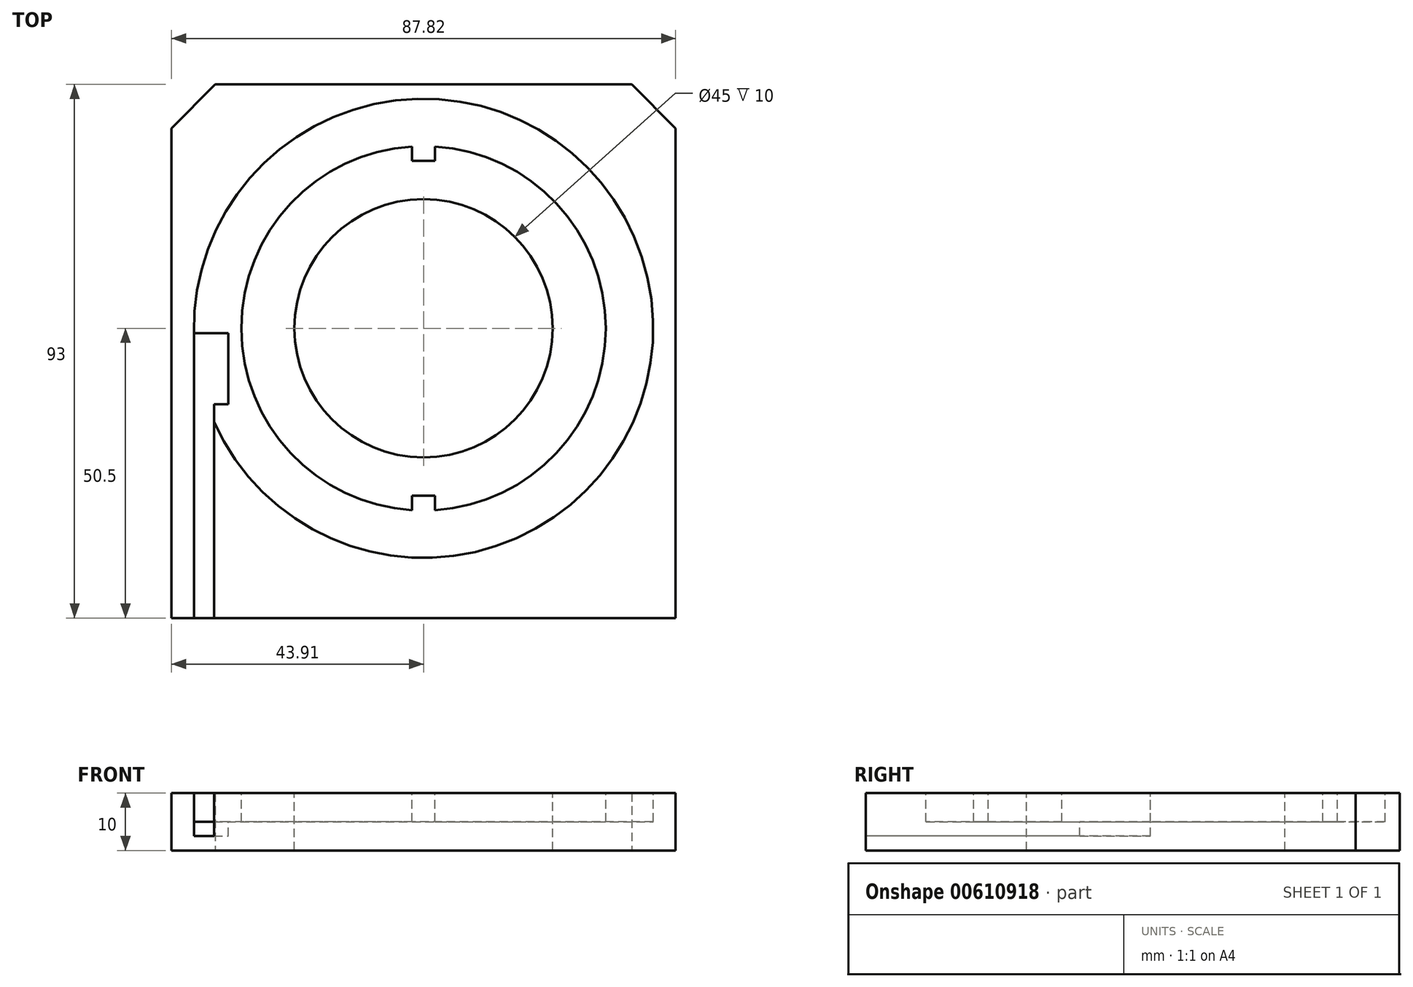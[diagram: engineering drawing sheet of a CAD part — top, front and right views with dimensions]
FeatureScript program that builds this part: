
annotation { "Feature Type Name" : "Feature", "Feature Type Description" : "" }
export const myFeature = defineFeature(function(context is Context, id is Id, definition is map)
    precondition{}
    {
        {
            var Q0;
            Q0=qCreatedBy(makeId("Top.planeOp"),FACE);
            var sketch = newSketch(context, id + "F0", { "sketchPlane" : qUnion([Q0])});
            skLineSegment(sketch, "E0.bottom", {"start": v(36.28, 46.5) * mm, "end": v(-36.28, 46.5) * mm});
            skLineSegment(sketch, "E0.top", {"start": v(43.92, -46.5) * mm, "end": v(-43.91, -46.5) * mm});
            skLineSegment(sketch, "E0.left", {"start": v(43.91, 38.86) * mm, "end": v(43.92, -46.5) * mm});
            skLineSegment(sketch, "E0.right", {"start": v(-43.92, 38.86) * mm, "end": v(-43.91, -46.5) * mm});
            skPoint(sketch, "E0.middle", {"position": v(0, 0) * mm});
            skLineSegment(sketch, "E1", {"start": v(-36.28, 46.5) * mm, "end": v(-43.92, 38.86) * mm});
            skLineSegment(sketch, "E2", {"start": v(36.28, 46.5) * mm, "end": v(43.92, 38.86) * mm});
            skPoint(sketch, "E3.orphan", {"position": v(-43.92, 46.5) * mm});
            skPoint(sketch, "E4.orphan", {"position": v(43.91, 46.5) * mm});
            skPoint(sketch, "E5.center.orphan", {"position": v(0, 4) * mm});
            skSolve(sketch);
        }
        {
            var Q0;
            Q0 = qSketchRegion(id + "F0", true);
            extrude(context, id + "F1", {"entities" : qUnion([Q0]), "depth" : 10 * mm, "offsetDistance" : 25 * mm});
        }
        {
            var Q0;
            Q0=makeQuery(id+"F1.opExtrude","CAP_FACE",FACE,{"disambiguationData":[OSD([sQuery(id+"F0.wireOp",EDGE,"E0.bottom"),sQuery(id+"F0.wireOp",EDGE,"E0.top"),sQuery(id+"F0.wireOp",EDGE,"E0.left"),sQuery(id+"F0.wireOp",EDGE,"E0.right"),sQuery(id+"F0.wireOp",EDGE,"E1"),sQuery(id+"F0.wireOp",EDGE,"E2")])],"isStart":false});
            var sketch = newSketch(context, id + "F2", { "sketchPlane" : qUnion([Q0])});
            skLineSegment(sketch, "E6", {"start": v(-43.92, 24) * mm, "end": v(43.91, 24) * mm, "construction": true});
            skCircle(sketch, "E7", {"center": v(0, 4) * mm, "radius": 20 * mm, "construction": true});
            skCircle(sketch, "E8", {"center": v(0, 4) * mm, "radius": 22.5 * mm});
            skCircle(sketch, "E9", {"center": v(0, 4) * mm, "radius": 40 * mm});
            skArc(sketch, "E10", {"start": v(2, -27.69) * mm, "mid": v(31.75, 4) * mm, "end": v(2, 35.69) * mm});
            skLineSegment(sketch, "E11", {"start": v(-2, 35.69) * mm, "end": v(-2, 33.15) * mm});
            skLineSegment(sketch, "E12", {"start": v(-2, 33.15) * mm, "end": v(2, 33.15) * mm});
            skLineSegment(sketch, "E13", {"start": v(2, 33.15) * mm, "end": v(2, 35.69) * mm});
            skLineSegment(sketch, "E14", {"start": v(0, 46.5) * mm, "end": v(0, -46.5) * mm, "construction": true});
            skLineSegment(sketch, "E15", {"start": v(-2, -27.69) * mm, "end": v(-2, -25.15) * mm});
            skLineSegment(sketch, "E16", {"start": v(-2, -25.15) * mm, "end": v(2, -25.15) * mm});
            skLineSegment(sketch, "E17", {"start": v(2, -25.15) * mm, "end": v(2, -27.69) * mm});
            skArc(sketch, "E18.trimOffspring", {"start": v(-2, 35.69) * mm, "mid": v(-31.75, 4) * mm, "end": v(-2, -27.69) * mm});
            skSolve(sketch);
        }
        {
            var Q0;
            Q0=makeQuery(id+"F2.imprint","IMPRINT",FACE,{"disambiguationData":[TD([[makeQuery(id+"F2.imprint","IMPRINT",EDGE,{"derivedFrom":sQuery(id+"F2.wireOp",EDGE,"E9")}),-1.0]])]});
            var sketch = newSketch(context, id + "F3", { "sketchPlane" : qUnion([Q0])});
            skLineSegment(sketch, "E19", {"start": v(-40, 3.11) * mm, "end": v(-40, -46.5) * mm, "construction": true});
            skLineSegment(sketch, "E20", {"start": v(-44.37, 3.11) * mm, "end": v(-20, 3.11) * mm, "construction": true});
            skLineSegment(sketch, "E21.top", {"start": v(-40, -46.5) * mm, "end": v(-36.52, -46.5) * mm});
            skLineSegment(sketch, "E21.left", {"start": v(-40, 3.11) * mm, "end": v(-40, -46.5) * mm});
            skLineSegment(sketch, "E21.right", {"start": v(-36.52, -9.2) * mm, "end": v(-36.52, -46.5) * mm});
            skLineSegment(sketch, "E22", {"start": v(-36.52, -9.2) * mm, "end": v(-34, -9.2) * mm});
            skLineSegment(sketch, "E23", {"start": v(-34, -9.2) * mm, "end": v(-34, 3.11) * mm});
            skLineSegment(sketch, "E24", {"start": v(-40, 3.11) * mm, "end": v(-34, 3.11) * mm});
            skPoint(sketch, "E25.end.orphan", {"position": v(-33.34, -110.36) * mm});
            skPoint(sketch, "E25.start.orphan", {"position": v(-40, -110.36) * mm});
            skSolve(sketch);
        }
        {
            var Q0;
            Q0 = qSketchRegion(id + "F3", true);
            extrude(context, id + "F4", {"entities" : qUnion([Q0]), "operationType" : NewBodyOperationType.REMOVE, "oppositeDirection" : true, "depth" : 7.5 * mm, "offsetDistance" : 25 * mm});
        }
        {
            var Q0;
            Q0=makeQuery(id+"F2.imprint","IMPRINT",FACE,{"disambiguationData":[TD([[makeQuery(id+"F2.imprint","IMPRINT",EDGE,{"derivedFrom":sQuery(id+"F2.wireOp",EDGE,"E8")}),1.0]])]});
            extrude(context, id + "F5", {"entities" : qUnion([Q0]), "operationType" : NewBodyOperationType.REMOVE, "endBound" : BoundingType.THROUGH_ALL, "oppositeDirection" : true, "depth" : 25 * mm, "offsetDistance" : 25 * mm});
        }
        {
            var Q0;
            Q0=makeQuery(id+"F2.imprint","IMPRINT",FACE,{"disambiguationData":[TD([[makeQuery(id+"F2.imprint","IMPRINT",EDGE,{"derivedFrom":sQuery(id+"F2.wireOp",EDGE,"E9")}),1.0]])]});
            extrude(context, id + "F6", {"entities" : qUnion([Q0]), "operationType" : NewBodyOperationType.REMOVE, "oppositeDirection" : true, "depth" : 5 * mm, "offsetDistance" : 25 * mm});
        }
    });
